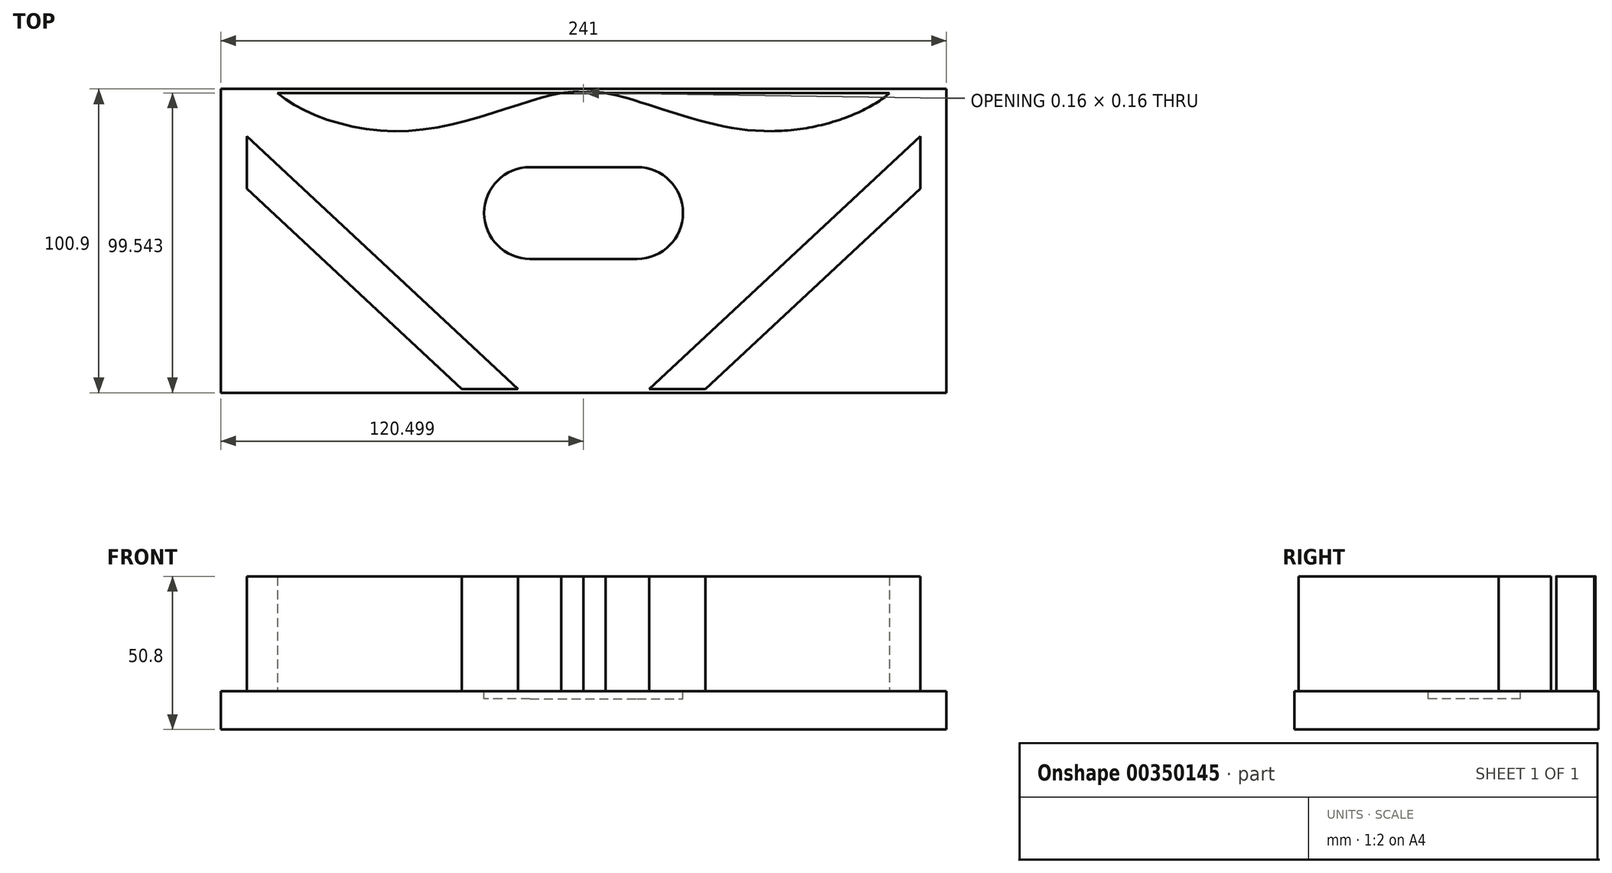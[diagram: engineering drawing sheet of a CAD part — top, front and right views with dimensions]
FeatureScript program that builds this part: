
annotation { "Feature Type Name" : "Feature", "Feature Type Description" : "" }
export const myFeature = defineFeature(function(context is Context, id is Id, definition is map)
    precondition{}
    {
        {
            var Q0;
            Q0=qCreatedBy(makeId("Top.planeOp"),FACE);
            var sketch = newSketch(context, id + "F0", { "sketchPlane" : qUnion([Q0])});
            skLineSegment(sketch, "E0", {"start": v(0, 88.9) * mm, "end": v(-57.15, 88.9) * mm});
            skLineSegment(sketch, "E1", {"start": v(-31.75, 0) * mm, "end": v(-111.85, 74.6) * mm});
            skLineSegment(sketch, "E2.MirrorCS", {"start": v(0, 88.9) * mm, "end": v(57.15, 88.9) * mm});
            skLineSegment(sketch, "E3.MirrorCS", {"start": v(31.75, 0) * mm, "end": v(111.85, 74.6) * mm});
            skLineSegment(sketch, "E4", {"start": v(-57.15, 88.9) * mm, "end": v(-101.6, 88.9) * mm});
            skLineSegment(sketch, "E5", {"start": v(57.15, 88.9) * mm, "end": v(101.6, 88.9) * mm});
            skFitSpline(sketch, "E6", {"points": [v(0, 88.9) * mm, v(-7.37, 88.9) * mm, v(-57.15, 76.46) * mm, v(-101.6, 88.9) * mm, v(-111.85, 105.09) * mm], "startDerivative": vector(15.35, 7.72) * mm, "endDerivative": vector(-32.75, 81.17) * mm});
            skFitSpline(sketch, "E7.MirrorCS", {"points": [v(0, 88.9) * mm, v(7.37, 88.9) * mm, v(57.15, 76.46) * mm, v(101.6, 88.9) * mm, v(111.85, 105.09) * mm], "startDerivative": vector(-14.17, 8.95) * mm, "endDerivative": vector(32.75, 81.17) * mm});
            skPoint(sketch, "E8", {"position": v(-111.85, 74.6) * mm});
            skPoint(sketch, "E9", {"position": v(111.85, 74.6) * mm});
            skFitSpline(sketch, "E10.MirrorCS", {"points": [v(0, 88.9) * mm, v(7.37, 88.9) * mm, v(57.15, 76.47) * mm, v(101.6, 88.9) * mm, v(111.85, 105.1) * mm], "startDerivative": vector(-15.35, 7.72) * mm, "endDerivative": vector(32.75, 81.17) * mm});
            skSolve(sketch);
        }
        {
            var Q0;
            Q0 = qSketchRegion(id + "F0", true);
            extrude(context, id + "F1", {"entities" : qUnion([Q0]), "depth" : 38.1 * mm});
        }
        {
            var Q0;
            Q0=sQuery(id+"F0.wireOp",EDGE,"E1");
            var Q1;
            Q1=sQuery(id+"F0.wireOp",EDGE,"E3.MirrorCS");
            extrude(context, id + "F2", {"bodyType" : ToolBodyType.SURFACE, "surfaceEntities" : qUnion([Q0, Q1]), "depth" : 38.1 * mm});
        }
        {
            var Q0;
            Q0=makeQuery(id+"F2.opExtrude","SWEPT_FACE",FACE,{"disambiguationData":[OSD([sQuery(id+"F0.wireOp",EDGE,"E3.MirrorCS")])]});
            extrude(context, id + "F3", {"entities" : qUnion([Q0]), "depth" : 12.7 * mm});
        }
        {
            var Q0;
            Q0=makeQuery(id+"F2.opExtrude","SWEPT_FACE",FACE,{"disambiguationData":[OSD([sQuery(id+"F0.wireOp",EDGE,"E1")])]});
            extrude(context, id + "F4", {"entities" : qUnion([Q0]), "oppositeDirection" : true, "depth" : 12.7 * mm});
        }
        {
            var Q0;
            {var subQ0=sQuery(id+"F0.wireOp",EDGE,"E1");Q0=makeQuery(id+"F4.opExtrude","SWEPT_FACE",FACE,{"disambiguationData":[OSD([subQ0]),TDD([makeQuery(id+"F2.opExtrude","CAP_EDGE",EDGE,{"disambiguationData":[OSD([subQ0])],"isStart":false})])]});}
            var sketch = newSketch(context, id + "F5", { "sketchPlane" : qUnion([Q0])});
            skLineSegment(sketch, "E11", {"start": v(-31.75, 0) * mm, "end": v(-21.77, -9.3) * mm});
            skLineSegment(sketch, "E12", {"start": v(-21.77, -9.3) * mm, "end": v(-40.4, -9.3) * mm});
            skLineSegment(sketch, "E13", {"start": v(-40.4, -9.3) * mm, "end": v(-31.75, 0) * mm});
            skSolve(sketch);
        }
        {
            var Q0;
            Q0 = qSketchRegion(id + "F5", true);
            extrude(context, id + "F6", {"entities" : qUnion([Q0]), "operationType" : NewBodyOperationType.ADD, "oppositeDirection" : true, "depth" : 38.1 * mm});
        }
        {
            var Q0;
            {var subQ0=sQuery(id+"F0.wireOp",EDGE,"E3.MirrorCS");Q0=makeQuery(id+"F3.opExtrude","SWEPT_FACE",FACE,{"disambiguationData":[OSD([subQ0]),TDD([makeQuery(id+"F2.opExtrude","CAP_EDGE",EDGE,{"disambiguationData":[OSD([subQ0])],"isStart":false})])]});}
            var sketch = newSketch(context, id + "F7", { "sketchPlane" : qUnion([Q0])});
            skLineSegment(sketch, "E14", {"start": v(31.75, 0) * mm, "end": v(21.77, -9.3) * mm});
            skLineSegment(sketch, "E15", {"start": v(21.77, -9.3) * mm, "end": v(40.4, -9.3) * mm});
            skLineSegment(sketch, "E16", {"start": v(40.4, -9.3) * mm, "end": v(31.75, 0) * mm});
            skSolve(sketch);
        }
        {
            var Q0;
            Q0 = qSketchRegion(id + "F7", true);
            extrude(context, id + "F8", {"entities" : qUnion([Q0]), "operationType" : NewBodyOperationType.ADD, "oppositeDirection" : true, "depth" : 38.1 * mm});
        }
        {
            var Q0;
            Q0=qCreatedBy(makeId("Top.planeOp"),FACE);
            var sketch = newSketch(context, id + "F9", { "sketchPlane" : qUnion([Q0])});
            skLineSegment(sketch, "E17.bottom", {"start": v(-120.5, 90.34) * mm, "end": v(120.5, 90.34) * mm});
            skLineSegment(sketch, "E17.top", {"start": v(-120.5, -10.56) * mm, "end": v(120.5, -10.56) * mm});
            skLineSegment(sketch, "E17.left", {"start": v(-120.5, 90.34) * mm, "end": v(-120.5, -10.56) * mm});
            skLineSegment(sketch, "E17.right", {"start": v(120.5, 90.34) * mm, "end": v(120.5, -10.56) * mm});
            skSolve(sketch);
        }
        {
            var Q0;
            Q0 = qSketchRegion(id + "F9", true);
            extrude(context, id + "F10", {"entities" : qUnion([Q0]), "oppositeDirection" : true, "depth" : 12.7 * mm});
        }
        {
            var Q0;
            Q0=makeQuery(id+"F10.opExtrude","CAP_FACE",FACE,{"disambiguationData":[OSD([sQuery(id+"F9.wireOp",EDGE,"E17.bottom"),sQuery(id+"F9.wireOp",EDGE,"E17.top"),sQuery(id+"F9.wireOp",EDGE,"E17.left"),sQuery(id+"F9.wireOp",EDGE,"E17.right")])],"isStart":true});
            var sketch = newSketch(context, id + "F11", { "sketchPlane" : qUnion([Q0])});
            skLineSegment(sketch, "E18", {"start": v(0, 0) * mm, "end": v(0, 76.86) * mm});
            skPoint(sketch, "E18.endSnap0", {"position": v(0, 90.34) * mm});
            skLineSegment(sketch, "E19", {"start": v(-17.78, 64.37) * mm, "end": v(17.78, 64.37) * mm});
            skLineSegment(sketch, "E20", {"start": v(-17.78, 33.89) * mm, "end": v(17.78, 33.89) * mm});
            skArc(sketch, "E21", {"start": v(-17.78, 64.37) * mm, "mid": v(-33.02, 49.13) * mm, "end": v(-17.78, 33.89) * mm});
            skArc(sketch, "E22", {"start": v(17.78, 64.37) * mm, "mid": v(33.02, 49.13) * mm, "end": v(17.78, 33.89) * mm});
            skSolve(sketch);
        }
        {
            var Q0;
            Q0 = qSketchRegion(id + "F11", true);
            extrude(context, id + "F12", {"entities" : qUnion([Q0]), "operationType" : NewBodyOperationType.REMOVE, "oppositeDirection" : true, "depth" : 2.54 * mm});
        }
        {
            var Q0;
            {var subQ0=sQuery(id+"F0.wireOp",EDGE,"E1");Q0=makeQuery(id+"F6.boolean.opBoolean","MERGE",FACE,{"derivedFrom":[makeQuery(id+"F4.opExtrude","SWEPT_FACE",FACE,{"disambiguationData":[OSD([subQ0]),TDD([makeQuery(id+"F2.opExtrude","CAP_EDGE",EDGE,{"disambiguationData":[OSD([subQ0])],"isStart":false})])]}),makeQuery(id+"F6.opExtrude","CAP_FACE",FACE,{"disambiguationData":[OSD([sQuery(id+"F5.wireOp",EDGE,"E11"),sQuery(id+"F5.wireOp",EDGE,"E12"),sQuery(id+"F5.wireOp",EDGE,"E13")])],"isStart":true})]});}
            var sketch = newSketch(context, id + "F13", { "sketchPlane" : qUnion([Q0])});
            skLineSegment(sketch, "E23", {"start": v(-111.85, 74.6) * mm, "end": v(-111.85, 57.25) * mm});
            skLineSegment(sketch, "E24", {"start": v(-111.85, 57.25) * mm, "end": v(-120.5, 65.31) * mm});
            skLineSegment(sketch, "E25", {"start": v(-120.5, 65.31) * mm, "end": v(-111.85, 74.6) * mm});
            skSolve(sketch);
        }
        {
            var Q0;
            Q0 = qSketchRegion(id + "F13", true);
            extrude(context, id + "F14", {"entities" : qUnion([Q0]), "operationType" : NewBodyOperationType.REMOVE, "oppositeDirection" : true, "depth" : 38.1 * mm});
        }
        {
            var Q0;
            {var subQ0=sQuery(id+"F0.wireOp",EDGE,"E3.MirrorCS");Q0=makeQuery(id+"F8.boolean.opBoolean","MERGE",FACE,{"derivedFrom":[makeQuery(id+"F3.opExtrude","SWEPT_FACE",FACE,{"disambiguationData":[OSD([subQ0]),TDD([makeQuery(id+"F2.opExtrude","CAP_EDGE",EDGE,{"disambiguationData":[OSD([subQ0])],"isStart":false})])]}),makeQuery(id+"F8.opExtrude","CAP_FACE",FACE,{"disambiguationData":[OSD([sQuery(id+"F7.wireOp",EDGE,"E14"),sQuery(id+"F7.wireOp",EDGE,"E15"),sQuery(id+"F7.wireOp",EDGE,"E16")])],"isStart":true})]});}
            var sketch = newSketch(context, id + "F15", { "sketchPlane" : qUnion([Q0])});
            skLineSegment(sketch, "E26", {"start": v(111.85, 74.6) * mm, "end": v(111.85, 57.25) * mm});
            skLineSegment(sketch, "E27", {"start": v(111.85, 57.25) * mm, "end": v(120.5, 65.31) * mm});
            skLineSegment(sketch, "E28", {"start": v(120.5, 65.31) * mm, "end": v(111.85, 74.6) * mm});
            skSolve(sketch);
        }
        {
            var Q0;
            Q0 = qSketchRegion(id + "F15", true);
            extrude(context, id + "F16", {"entities" : qUnion([Q0]), "operationType" : NewBodyOperationType.REMOVE, "oppositeDirection" : true, "depth" : 38.1 * mm});
        }
    });
